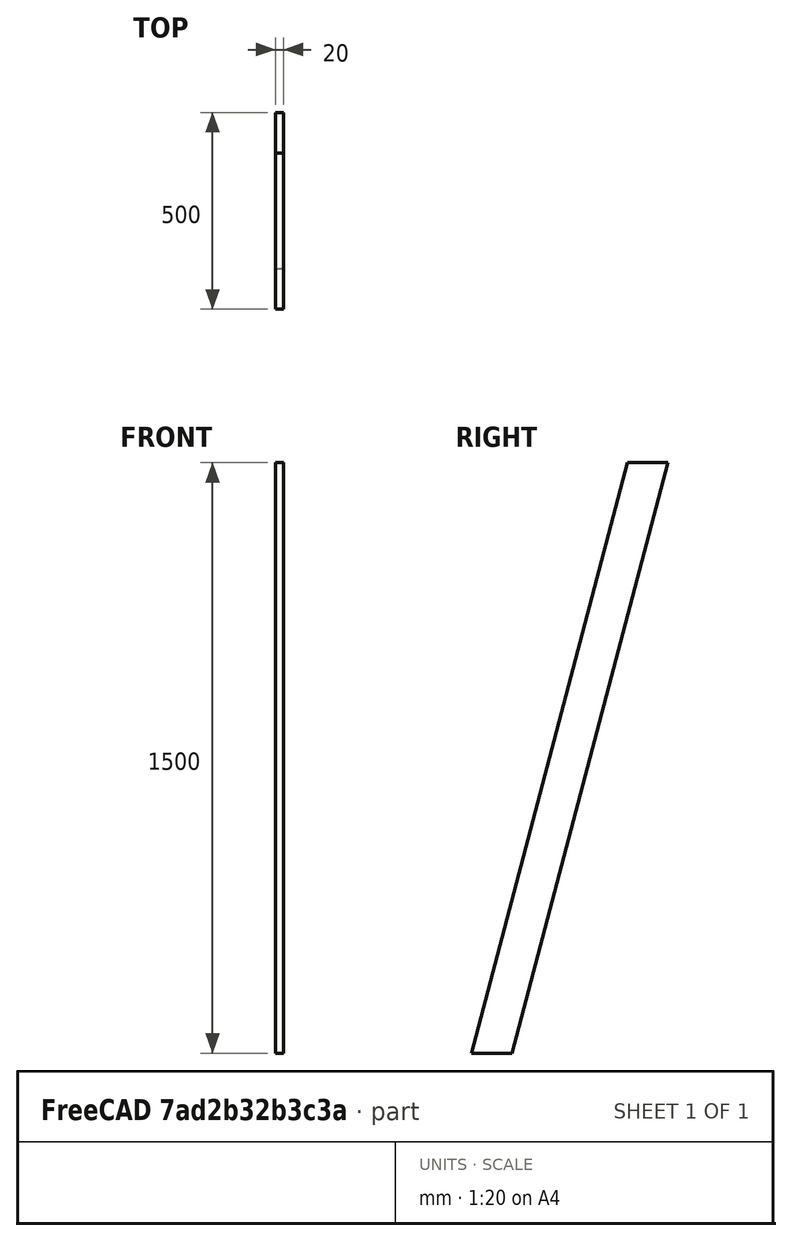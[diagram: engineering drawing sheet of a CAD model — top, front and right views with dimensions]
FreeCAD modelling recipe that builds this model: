
FCSTD DOCUMENT  (FreeCAD 0.18R4 (GitTag))
Label: aframe-2
License: All rights reserved
LicenseURL: http://en.wikipedia.org/wiki/All_rights_reserved
objects: Sketcher::SketchObject×1, PartDesign::Pad×1, PartDesign::Body×1, App::Part×1
note: 4 computed .brp shape members not serialized (recipe doc carries the construction recipe); baked Part::Feature solids carry a one-line shape summary decoded from their .brp

FEATURE [Sketcher::SketchObject] Sketch
  MapMode = 5
  Placement = pos=(0,0,0) rot=(0.57735,0.57735,0.57735;2.0944rad)
  Support = -> [YZ_Plane001]
  sketch-geometry (4):
    g0: LineSegment StartX=-103.5 StartY=1500 StartZ=0 EndX=0 EndY=1500 EndZ=0
    g1: LineSegment StartX=0 StartY=1500 StartZ=0 EndX=-396.5 EndY=0 EndZ=0
    g2: LineSegment StartX=-396.5 StartY=0 StartZ=0 EndX=-500 EndY=-0.00270184 EndZ=0
    g3: LineSegment StartX=-500 StartY=-0.00270184 StartZ=0 EndX=-103.5 EndY=1500 EndZ=0
  constraints (11):
    c: Coincident(g0,g1)
    c: Horizontal(g0)
    c: PointOnObject(g0,g-2)
    c: PointOnObject(g1,g-1)
    c: Distance(g0,g-1) = 1500
    c: Equal(g2,g0)
    c: Coincident(g3,g0)
    c: Coincident(g3,g2)
    c: Coincident(g1,g2)
    c: Distance(g2,g-1) = 500
    c: Distance(g2) = 103.5
FEATURE [PartDesign::Pad] Pad
  Length = 20
  Length2 = 100
  Placement = pos=(0,0,0) rot=(0.57735,0.57735,0.57735;2.0944rad)
  Profile = -> Sketch
  Type = 0
FEATURE [PartDesign::Body] Body
  Group = -> [Sketch,Pad]
  Origin = -> Origin001
  Tip = -> Pad
FEATURE [App::Part] Part
  Group = -> [Body]
  Origin = -> Origin
